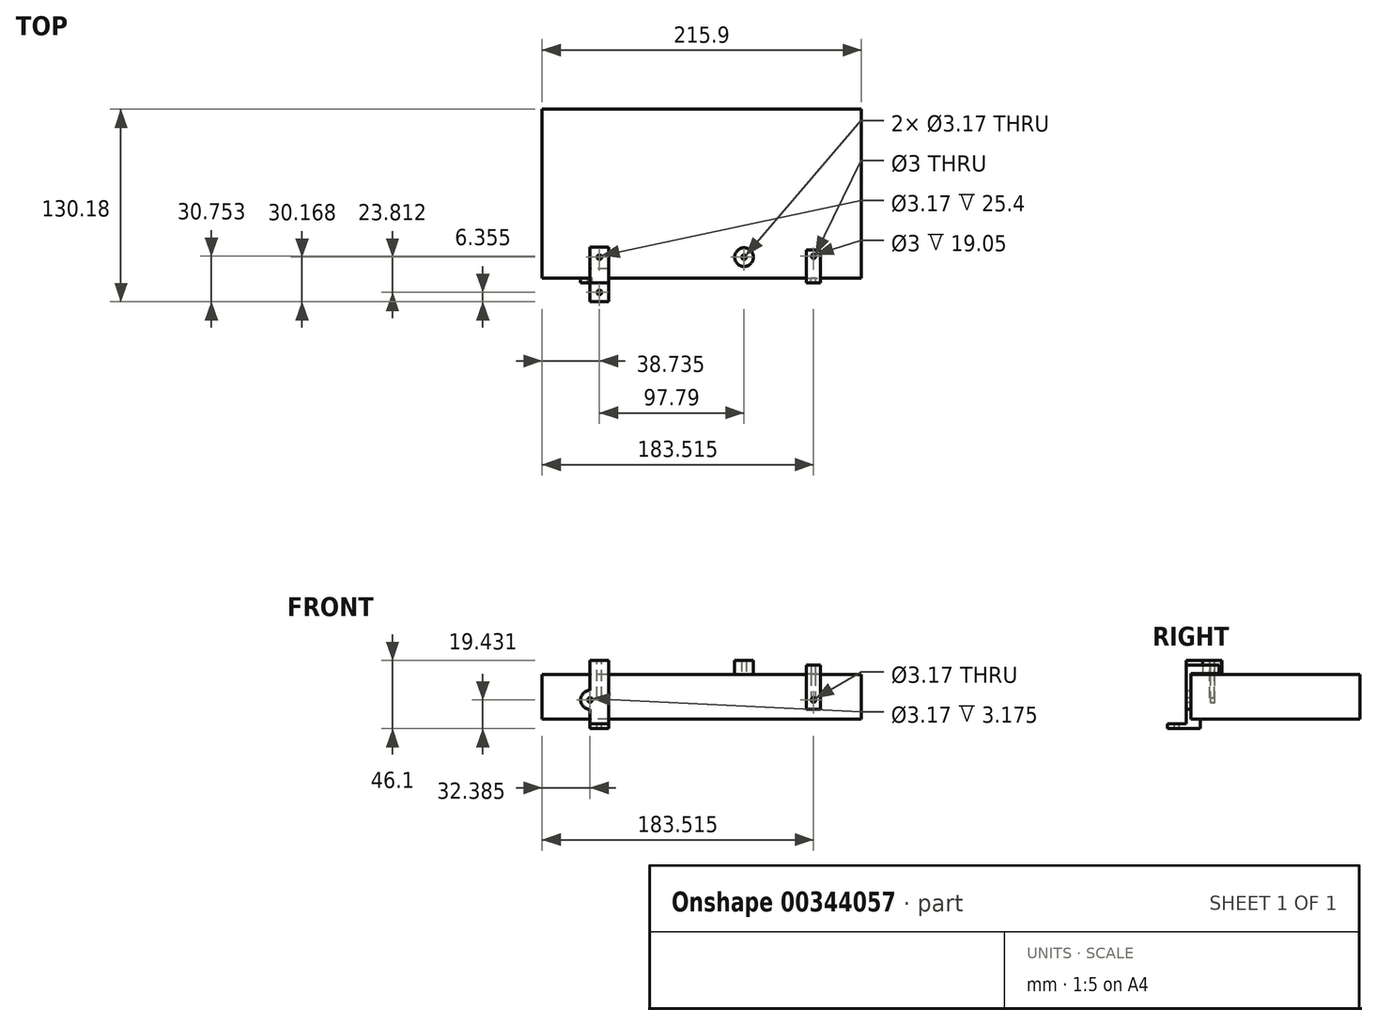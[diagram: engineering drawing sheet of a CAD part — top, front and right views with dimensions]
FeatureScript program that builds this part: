
annotation { "Feature Type Name" : "Feature", "Feature Type Description" : "" }
export const myFeature = defineFeature(function(context is Context, id is Id, definition is map)
    precondition{}
    {
        {
            var Q0;
            Q0=qCreatedBy(makeId("Top.planeOp"),FACE);
            var sketch = newSketch(context, id + "F0", { "sketchPlane" : qUnion([Q0])});
            skLineSegment(sketch, "E0.bottom", {"start": v(107.95, -57.15) * mm, "end": v(-107.95, -57.15) * mm});
            skLineSegment(sketch, "E0.top", {"start": v(107.95, 57.15) * mm, "end": v(-107.95, 57.15) * mm});
            skLineSegment(sketch, "E0.left", {"start": v(107.95, -57.15) * mm, "end": v(107.95, 57.15) * mm});
            skLineSegment(sketch, "E0.right", {"start": v(-107.95, -57.15) * mm, "end": v(-107.95, 57.15) * mm});
            skPoint(sketch, "E0.middle", {"position": v(0, 0) * mm});
            skSolve(sketch);
        }
        {
            var Q0;
            Q0=makeQuery(id+"F0.imprint","IMPRINT",FACE,{"disambiguationData":[TD([[makeQuery(id+"F0.imprint","IMPRINT",EDGE,{"derivedFrom":sQuery(id+"F0.wireOp",EDGE,"E0.bottom")}),-1.0]])]});
            extrude(context, id + "F1", {"entities" : qUnion([Q0]), "depth" : 30.23 * mm});
        }
        {
            var Q0;
            Q0=makeQuery(id+"F1.opExtrude","SWEPT_FACE",FACE,{"disambiguationData":[OSD([sQuery(id+"F0.wireOp",EDGE,"E0.bottom")])]});
            var sketch = newSketch(context, id + "F2", { "sketchPlane" : qUnion([Q0])});
            skLineSegment(sketch, "E1.bottom", {"start": v(-107.95, 30.23) * mm, "end": v(-75.57, 30.23) * mm});
            skLineSegment(sketch, "E1.top", {"start": v(-107.95, 13.08) * mm, "end": v(-75.57, 13.08) * mm});
            skLineSegment(sketch, "E1.left", {"start": v(-107.95, 30.23) * mm, "end": v(-107.95, 13.08) * mm});
            skLineSegment(sketch, "E1.right", {"start": v(-75.57, 30.23) * mm, "end": v(-75.57, 13.08) * mm});
            skPoint(sketch, "E2", {"position": v(-75.57, 13.08) * mm});
            skPoint(sketch, "E3.MirrorP", {"position": v(75.57, 13.08) * mm});
            skSolve(sketch);
        }
        {
            var Q0;
            Q0=makeQuery(id+"F1.opExtrude","CAP_FACE",FACE,{"disambiguationData":[OSD([sQuery(id+"F0.wireOp",EDGE,"E0.bottom"),sQuery(id+"F0.wireOp",EDGE,"E0.top"),sQuery(id+"F0.wireOp",EDGE,"E0.left"),sQuery(id+"F0.wireOp",EDGE,"E0.right")])],"isStart":false});
            var sketch = newSketch(context, id + "F3", { "sketchPlane" : qUnion([Q0])});
            skLineSegment(sketch, "E4.bottom", {"start": v(-69.22, 42.86) * mm, "end": v(28.58, 42.86) * mm});
            skLineSegment(sketch, "E4.top", {"start": v(-69.22, -42.86) * mm, "end": v(28.58, -42.86) * mm});
            skLineSegment(sketch, "E4.left", {"start": v(-69.22, 42.86) * mm, "end": v(-69.22, -42.86) * mm});
            skLineSegment(sketch, "E4.right", {"start": v(28.58, 42.86) * mm, "end": v(28.58, -42.86) * mm});
            skPoint(sketch, "E5", {"position": v(-69.22, 0) * mm});
            skPoint(sketch, "E6.0", {"position": v(-75.57, -57.15) * mm});
            skSolve(sketch);
        }
        {
            var Q0;
            {var subQ3=sQuery(id+"F2.wireOp",EDGE,"E1.top");Q0=makeQuery(id+"F2.imprint","IMPRINT",FACE,{"disambiguationData":[TD([[makeQuery(id+"F2.imprint","IMPRINT",EDGE,{"derivedFrom":subQ3}),-1.0]])]});}
            var sketch = newSketch(context, id + "F4", { "sketchPlane" : qUnion([Q0])});
            skPoint(sketch, "E7.0", {"position": v(-75.57, 13.08) * mm});
            skLineSegment(sketch, "E8.bottom", {"start": v(-75.57, -6.35) * mm, "end": v(-62.87, -6.35) * mm});
            skLineSegment(sketch, "E8.top", {"start": v(-75.57, 39.75) * mm, "end": v(-62.87, 39.75) * mm});
            skLineSegment(sketch, "E8.left", {"start": v(-75.57, -6.35) * mm, "end": v(-75.57, 39.75) * mm});
            skLineSegment(sketch, "E8.right", {"start": v(-62.87, -6.35) * mm, "end": v(-62.87, 39.75) * mm});
            skPoint(sketch, "E9.0", {"position": v(-107.95, 30.23) * mm});
            skPoint(sketch, "E10.0", {"position": v(-107.95, 0) * mm});
            skCircle(sketch, "E11", {"center": v(-75.57, 13.08) * mm, "radius": 6.35 * mm});
            skCircle(sketch, "E12", {"center": v(-75.57, 13.08) * mm, "radius": 1.59 * mm});
            skSolve(sketch);
        }
        {
            var Q0;
            {var subQ0=sQuery(id+"F4.wireOp",EDGE,"E11");var subQ1=sQuery(id+"F4.wireOp",EDGE,"E8.left");var subQ3=makeQuery(id+"F4.imprint","INTERSECT",VERTEX,{"disambiguationData":[OD(1.0)],"derivedFrom":[subQ1,subQ0]});Q0=makeQuery(id+"F4.imprint","IMPRINT",FACE,{"disambiguationData":[TD([[makeQuery(id+"F4.imprint","IMPRINT",EDGE,{"disambiguationData":[TD([[subQ3,1.0]])],"derivedFrom":subQ1}),-1.0]])]});}
            var Q1;
            {var subQ0=sQuery(id+"F4.wireOp",EDGE,"E11");var subQ1=sQuery(id+"F4.wireOp",EDGE,"E8.left");var subQ2=makeQuery(id+"F4.imprint","INTERSECT",VERTEX,{"disambiguationData":[OD(1.0)],"derivedFrom":[subQ1,subQ0]});Q1=makeQuery(id+"F4.imprint","IMPRINT",FACE,{"disambiguationData":[TD([[makeQuery(id+"F4.imprint","IMPRINT",EDGE,{"disambiguationData":[TD([[subQ2,-1.0]])],"derivedFrom":subQ1}),-1.0]])]});}
            var Q2;
            {var subQ0=sQuery(id+"F4.wireOp",EDGE,"E11");var subQ1=sQuery(id+"F4.wireOp",EDGE,"E8.left");var subQ2=makeQuery(id+"F4.imprint","INTERSECT",VERTEX,{"disambiguationData":[OD(0.0)],"derivedFrom":[subQ1,subQ0]});Q2=makeQuery(id+"F4.imprint","IMPRINT",FACE,{"disambiguationData":[TD([[makeQuery(id+"F4.imprint","IMPRINT",EDGE,{"disambiguationData":[TD([[subQ2,-1.0]])],"derivedFrom":subQ1}),-1.0]])]});}
            var Q3;
            {var subQ0=sQuery(id+"F4.wireOp",EDGE,"E11");var subQ1=sQuery(id+"F4.wireOp",EDGE,"E8.left");var subQ2=makeQuery(id+"F4.imprint","INTERSECT",VERTEX,{"disambiguationData":[OD(1.0)],"derivedFrom":[subQ1,subQ0]});Q3=makeQuery(id+"F4.imprint","IMPRINT",FACE,{"disambiguationData":[TD([[makeQuery(id+"F4.imprint","IMPRINT",EDGE,{"disambiguationData":[TD([[subQ2,-1.0]])],"derivedFrom":subQ1}),1.0]])]});}
            var Q4;
            {var subQ0=sQuery(id+"F4.wireOp",EDGE,"E8.bottom");Q4=makeQuery(id+"F4.imprint","IMPRINT",FACE,{"disambiguationData":[TD([[makeQuery(id+"F4.imprint","IMPRINT",EDGE,{"derivedFrom":subQ0}),1.0]])]});}
            var Q5;
            {var subQ0=sQuery(id+"F4.wireOp",EDGE,"E8.top");Q5=makeQuery(id+"F4.imprint","IMPRINT",FACE,{"disambiguationData":[TD([[makeQuery(id+"F4.imprint","IMPRINT",EDGE,{"derivedFrom":subQ0}),-1.0]])]});}
            extrude(context, id + "F5", {"entities" : qUnion([Q0, Q1, Q2, Q3, Q4, Q5]), "depth" : 3.17 * mm});
        }
        {
            var Q0;
            Q0=makeQuery(id+"F5.opExtrude","CAP_FACE",FACE,{"disambiguationData":[OSD([sQuery(id+"F4.wireOp",EDGE,"E8.bottom"),sQuery(id+"F4.wireOp",EDGE,"E8.top"),sQuery(id+"F4.wireOp",EDGE,"E8.left"),sQuery(id+"F4.wireOp",EDGE,"E8.right"),sQuery(id+"F4.wireOp",EDGE,"E11"),sQuery(id+"F4.wireOp",EDGE,"E12")])],"isStart":true});
            var sketch = newSketch(context, id + "F6", { "sketchPlane" : qUnion([Q0])});
            skLineSegment(sketch, "E13.0", {"start": v(-107.95, 30.23) * mm, "end": v(107.95, 30.23) * mm});
            skLineSegment(sketch, "E14.0", {"start": v(75.57, 39.75) * mm, "end": v(75.57, 19.43) * mm});
            skLineSegment(sketch, "E15.0", {"start": v(62.87, -6.35) * mm, "end": v(62.87, 39.75) * mm});
            skLineSegment(sketch, "E16.0", {"start": v(75.57, 39.75) * mm, "end": v(62.87, 39.75) * mm});
            skLineSegment(sketch, "E17.0", {"start": v(75.57, -6.35) * mm, "end": v(75.57, 6.73) * mm});
            skLineSegment(sketch, "E18.0", {"start": v(75.57, -6.35) * mm, "end": v(62.87, -6.35) * mm});
            skLineSegment(sketch, "E19.0", {"start": v(-107.95, 0) * mm, "end": v(107.95, 0) * mm});
            skSolve(sketch);
        }
        {
            var Q0;
            {var subQ0=sQuery(id+"F6.wireOp",EDGE,"E18.0");Q0=makeQuery(id+"F6.imprint","IMPRINT",FACE,{"disambiguationData":[TD([[makeQuery(id+"F6.imprint","IMPRINT",EDGE,{"derivedFrom":subQ0}),-1.0]])]});}
            extrude(context, id + "F7", {"entities" : qUnion([Q0]), "operationType" : NewBodyOperationType.ADD, "depth" : 6.35 * mm});
        }
        {
            var Q0;
            {var subQ5=sQuery(id+"F6.wireOp",EDGE,"E16.0");Q0=makeQuery(id+"F6.imprint","IMPRINT",FACE,{"disambiguationData":[TD([[makeQuery(id+"F6.imprint","IMPRINT",EDGE,{"derivedFrom":subQ5}),1.0]])]});}
            extrude(context, id + "F8", {"entities" : qUnion([Q0]), "operationType" : NewBodyOperationType.ADD, "depth" : 20.95 * mm});
        }
        {
            var Q0;
            Q0=makeQuery(id+"F5.opExtrude","CAP_FACE",FACE,{"disambiguationData":[OSD([sQuery(id+"F4.wireOp",EDGE,"E8.bottom"),sQuery(id+"F4.wireOp",EDGE,"E8.top"),sQuery(id+"F4.wireOp",EDGE,"E8.left"),sQuery(id+"F4.wireOp",EDGE,"E8.right"),sQuery(id+"F4.wireOp",EDGE,"E11"),sQuery(id+"F4.wireOp",EDGE,"E12")])],"isStart":false});
            var sketch = newSketch(context, id + "F9", { "sketchPlane" : qUnion([Q0])});
            skLineSegment(sketch, "E20.bottom", {"start": v(-75.57, -6.35) * mm, "end": v(-62.87, -6.35) * mm});
            skLineSegment(sketch, "E20.top", {"start": v(-75.57, -3.18) * mm, "end": v(-62.87, -3.18) * mm});
            skLineSegment(sketch, "E20.left", {"start": v(-75.57, -6.35) * mm, "end": v(-75.57, -3.18) * mm});
            skLineSegment(sketch, "E20.right", {"start": v(-62.87, -6.35) * mm, "end": v(-62.87, -3.18) * mm});
            skSolve(sketch);
        }
        {
            var Q0;
            Q0=makeQuery(id+"F9.imprint","IMPRINT",FACE,{"disambiguationData":[TD([[makeQuery(id+"F9.imprint","IMPRINT",EDGE,{"derivedFrom":sQuery(id+"F9.wireOp",EDGE,"E20.bottom")}),1.0]])]});
            extrude(context, id + "F10", {"entities" : qUnion([Q0]), "operationType" : NewBodyOperationType.ADD, "depth" : 12.7 * mm});
        }
        {
            var Q0;
            Q0=makeQuery(id+"F10.opExtrude","SWEPT_FACE",FACE,{"disambiguationData":[OSD([sQuery(id+"F9.wireOp",EDGE,"E20.top")])]});
            var sketch = newSketch(context, id + "F11", { "sketchPlane" : qUnion([Q0])});
            skCircle(sketch, "E21", {"center": v(-69.22, -66.67) * mm, "radius": 1.59 * mm});
            skPoint(sketch, "E21.centerSnap0", {"position": v(-62.87, -66.67) * mm});
            skPoint(sketch, "E21.centerSnap1", {"position": v(-69.22, -73.02) * mm});
            skSolve(sketch);
        }
        {
            var Q0;
            Q0=makeQuery(id+"F11.imprint","IMPRINT",FACE,{"disambiguationData":[TD([[makeQuery(id+"F11.imprint","IMPRINT",EDGE,{"derivedFrom":sQuery(id+"F11.wireOp",EDGE,"E21")}),1.0]])]});
            extrude(context, id + "F12", {"entities" : qUnion([Q0]), "operationType" : NewBodyOperationType.REMOVE, "oppositeDirection" : true, "depth" : 25.4 * mm});
        }
        {
            var Q0;
            Q0=makeQuery(id+"F8.boolean.opBoolean","MERGE",FACE,{"derivedFrom":[makeQuery(id+"F5.opExtrude","SWEPT_FACE",FACE,{"disambiguationData":[OSD([sQuery(id+"F4.wireOp",EDGE,"E8.top")])]}),makeQuery(id+"F8.opExtrude","SWEPT_FACE",FACE,{"disambiguationData":[OSD([sQuery(id+"F6.wireOp",EDGE,"E16.0")])]})]});
            var sketch = newSketch(context, id + "F13", { "sketchPlane" : qUnion([Q0])});
            skPoint(sketch, "E22.0", {"position": v(-69.22, -42.86) * mm});
            skCircle(sketch, "E23", {"center": v(-69.22, -42.86) * mm, "radius": 1.59 * mm});
            skSolve(sketch);
        }
        {
            var Q0;
            Q0=makeQuery(id+"F13.imprint","IMPRINT",FACE,{"disambiguationData":[TD([[makeQuery(id+"F13.imprint","IMPRINT",EDGE,{"derivedFrom":sQuery(id+"F13.wireOp",EDGE,"E23")}),1.0]])]});
            extrude(context, id + "F14", {"entities" : qUnion([Q0]), "operationType" : NewBodyOperationType.REMOVE, "oppositeDirection" : true, "depth" : 25.4 * mm});
        }
        {
            var Q0;
            Q0=makeQuery(id+"F3.imprint","IMPRINT",FACE,{"disambiguationData":[TD([[makeQuery(id+"F3.imprint","IMPRINT",EDGE,{"derivedFrom":sQuery(id+"F3.wireOp",EDGE,"E4.bottom")}),1.0]])]});
            var sketch = newSketch(context, id + "F15", { "sketchPlane" : qUnion([Q0])});
            skLineSegment(sketch, "E24.bottom", {"start": v(42.55, -42.45) * mm, "end": v(96.52, -42.45) * mm});
            skLineSegment(sketch, "E24.top", {"start": v(42.55, -18.32) * mm, "end": v(96.52, -18.32) * mm});
            skLineSegment(sketch, "E24.left", {"start": v(42.55, -42.45) * mm, "end": v(42.55, -18.32) * mm});
            skLineSegment(sketch, "E24.right", {"start": v(96.52, -42.45) * mm, "end": v(96.52, -18.32) * mm});
            skLineSegment(sketch, "E25.bottom", {"start": v(51.44, -39.27) * mm, "end": v(86.36, -39.27) * mm});
            skLineSegment(sketch, "E25.top", {"start": v(51.44, -21.5) * mm, "end": v(86.36, -21.5) * mm});
            skLineSegment(sketch, "E25.left", {"start": v(51.44, -39.27) * mm, "end": v(51.44, -21.5) * mm});
            skLineSegment(sketch, "E25.right", {"start": v(86.36, -39.27) * mm, "end": v(86.36, -21.5) * mm});
            skSolve(sketch);
        }
        {
            var Q0;
            Q0=makeQuery(id+"F3.imprint","IMPRINT",FACE,{"disambiguationData":[TD([[makeQuery(id+"F3.imprint","IMPRINT",EDGE,{"derivedFrom":sQuery(id+"F3.wireOp",EDGE,"E4.bottom")}),1.0]])]});
            var sketch = newSketch(context, id + "F16", { "sketchPlane" : qUnion([Q0])});
            skPoint(sketch, "E26.0", {"position": v(28.58, -42.86) * mm});
            skCircle(sketch, "E27", {"center": v(28.58, -42.86) * mm, "radius": 6.35 * mm});
            skCircle(sketch, "E28", {"center": v(28.58, -42.86) * mm, "radius": 1.59 * mm});
            skSolve(sketch);
        }
        {
            var Q0;
            {var subQ0=sQuery(id+"F16.wireOp",EDGE,"E27");var subQ1=makeQuery(id+"F3.imprint","IMPRINT",EDGE,{"derivedFrom":sQuery(id+"F3.wireOp",EDGE,"E4.top")});var subQ2=makeQuery(id+"F16.imprint","INTERSECT",VERTEX,{"derivedFrom":[subQ1,subQ0]});Q0=makeQuery(id+"F16.imprint","IMPRINT",FACE,{"disambiguationData":[TD([[makeQuery(id+"F16.imprint","IMPRINT",EDGE,{"disambiguationData":[TD([[subQ2,-1.0]])],"derivedFrom":subQ0}),1.0]])]});}
            var Q1;
            {var subQ0=sQuery(id+"F16.wireOp",EDGE,"E27");var subQ1=makeQuery(id+"F3.imprint","IMPRINT",EDGE,{"derivedFrom":sQuery(id+"F3.wireOp",EDGE,"E4.top")});var subQ2=makeQuery(id+"F16.imprint","INTERSECT",VERTEX,{"derivedFrom":[subQ1,subQ0]});Q1=makeQuery(id+"F16.imprint","IMPRINT",FACE,{"disambiguationData":[TD([[makeQuery(id+"F16.imprint","IMPRINT",EDGE,{"disambiguationData":[TD([[subQ2,1.0]])],"derivedFrom":subQ0}),1.0]])]});}
            extrude(context, id + "F17", {"entities" : qUnion([Q0, Q1]), "depth" : 9.52 * mm});
        }
        {
            var Q0;
            {var subQ1=sQuery(id+"F0.wireOp",EDGE,"E0.bottom");var subQ5=makeQuery(id+"F1.opExtrude","SWEPT_EDGE",EDGE,{"disambiguationData":[OSD([subQ1,sQuery(id+"F0.wireOp",EDGE,"E0.left")])]});var subQ8=makeQuery(id+"F2.imprint","IMPRINT",EDGE,{"derivedFrom":subQ5});Q0=makeQuery(id+"F4.imprint","IMPRINT",FACE,{"disambiguationData":[TD([[makeQuery(id+"F4.imprint","IMPRINT",EDGE,{"derivedFrom":subQ8}),-1.0]])]});}
            var sketch = newSketch(context, id + "F18", { "sketchPlane" : qUnion([Q0])});
            skLineSegment(sketch, "E29.bottom", {"start": v(70.8, 6.73) * mm, "end": v(80.33, 6.73) * mm});
            skLineSegment(sketch, "E29.top", {"start": v(70.8, 36.58) * mm, "end": v(80.33, 36.58) * mm});
            skLineSegment(sketch, "E29.left", {"start": v(70.8, 6.73) * mm, "end": v(70.8, 36.58) * mm});
            skLineSegment(sketch, "E29.right", {"start": v(80.33, 6.73) * mm, "end": v(80.33, 36.58) * mm});
            skPoint(sketch, "E30", {"position": v(75.57, 6.73) * mm});
            skLineSegment(sketch, "E31", {"start": v(70.8, 30.86) * mm, "end": v(80.33, 30.86) * mm});
            skPoint(sketch, "E32.0", {"position": v(75.57, 13.08) * mm});
            skCircle(sketch, "E33", {"center": v(75.57, 13.08) * mm, "radius": 1.59 * mm});
            skSolve(sketch);
        }
        {
            var Q0;
            {var subQ1=sQuery(id+"F18.wireOp",EDGE,"E29.bottom");Q0=makeQuery(id+"F18.imprint","IMPRINT",FACE,{"disambiguationData":[TD([[makeQuery(id+"F18.imprint","IMPRINT",EDGE,{"derivedFrom":subQ1}),1.0]])]});}
            var Q1;
            {var subQ0=sQuery(id+"F18.wireOp",EDGE,"E29.top");Q1=makeQuery(id+"F18.imprint","IMPRINT",FACE,{"disambiguationData":[TD([[makeQuery(id+"F18.imprint","IMPRINT",EDGE,{"derivedFrom":subQ0}),-1.0]])]});}
            var Q2;
            {var subQ0=sQuery(id+"F18.wireOp",EDGE,"E31");Q2=makeQuery(id+"F18.imprint","IMPRINT",FACE,{"disambiguationData":[TD([[makeQuery(id+"F18.imprint","IMPRINT",EDGE,{"derivedFrom":subQ0}),-1.0]])]});}
            extrude(context, id + "F19", {"entities" : qUnion([Q0, Q1, Q2]), "depth" : 3.17 * mm});
        }
        {
            var Q0;
            {var subQ0=sQuery(id+"F18.wireOp",EDGE,"E29.top");Q0=makeQuery(id+"F18.imprint","IMPRINT",FACE,{"disambiguationData":[TD([[makeQuery(id+"F18.imprint","IMPRINT",EDGE,{"derivedFrom":subQ0}),-1.0]])]});}
            extrude(context, id + "F20", {"entities" : qUnion([Q0]), "operationType" : NewBodyOperationType.ADD, "oppositeDirection" : true, "depth" : 19.05 * mm});
        }
        {
            var Q0;
            {var subQ0=sQuery(id+"F18.wireOp",EDGE,"E29.top");Q0=makeQuery(id+"F20.boolean.opBoolean","MERGE",FACE,{"derivedFrom":[makeQuery(id+"F19.opExtrude","SWEPT_FACE",FACE,{"disambiguationData":[OSD([subQ0])]}),makeQuery(id+"F20.opExtrude","SWEPT_FACE",FACE,{"disambiguationData":[OSD([subQ0])]})]});}
            var sketch = newSketch(context, id + "F21", { "sketchPlane" : qUnion([Q0])});
            skCircle(sketch, "E34", {"center": v(75.57, -42.28) * mm, "radius": 1.5 * mm});
            skPoint(sketch, "E34.centerSnap0", {"position": v(75.57, -38.1) * mm});
            skSolve(sketch);
        }
        {
            var Q0;
            Q0=makeQuery(id+"F21.imprint","IMPRINT",FACE,{"disambiguationData":[TD([[makeQuery(id+"F21.imprint","IMPRINT",EDGE,{"derivedFrom":sQuery(id+"F21.wireOp",EDGE,"E34")}),1.0]])]});
            extrude(context, id + "F22", {"entities" : qUnion([Q0]), "operationType" : NewBodyOperationType.REMOVE, "oppositeDirection" : true, "depth" : 25.4 * mm});
        }
    });
